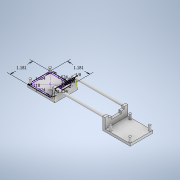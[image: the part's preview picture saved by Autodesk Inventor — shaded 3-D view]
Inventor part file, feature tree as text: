
AUTODESK INVENTOR PART (.ipt)
format: ipt  version: 2020 (Build 240168000, 168)  size: 195,072 bytes
history: native  units: in
note: dims shown in document units (in); Inventor stores cm internally (conversion verified against a paired STEP export)
features: extrude x6, sketch x4, mirror x1
ambient origin geometry x8: Origin, YZ Plane, XZ Plane, XY Plane, X Axis, Y Axis, Z Axis, Center Point
bodies: Solid1 (feature_tree)
feature tree (11):
  sketch  "Sketch1"  dims[d0=1.1811in d1=1.1811in]
  extrude  "Extrusion1"  Depth=1.1811in
  extrude  "Extrusion2"  Depth=1.0236in
  extrude  "Extrusion3"  Depth=0.7874in
  extrude  "Extrusion4"  Depth=0.25in TaperAngle=0.0deg
  sketch  "Sketch4"  dims[d13=0.125in d14=0.0in d15=0.25in d16=0.0in d17=0.25in d18=0.0in d19=0.125in d20=0.5187in d21=0.0in d22=0.0625in d23=0.5in d24=90.0deg d25=1.0in d26=0.125in d27=0.125in d28=1.25in d29=0.0in d30=0.125in d31=0.0in]
  extrude  "Extrusion5"  Depth=0.25in TaperAngle=0.0deg
  extrude  "Extrusion6"  Depth=0.125in
  mirror  "Mirror1"
  sketch  "Sketch2"  dims[d2=1.0236in d3=1.0236in]
  sketch  "Sketch3"  dims[d4=0.1181in d5=0.7874in d7=1.0236in d8=0.7874in d10=1.0236in]
